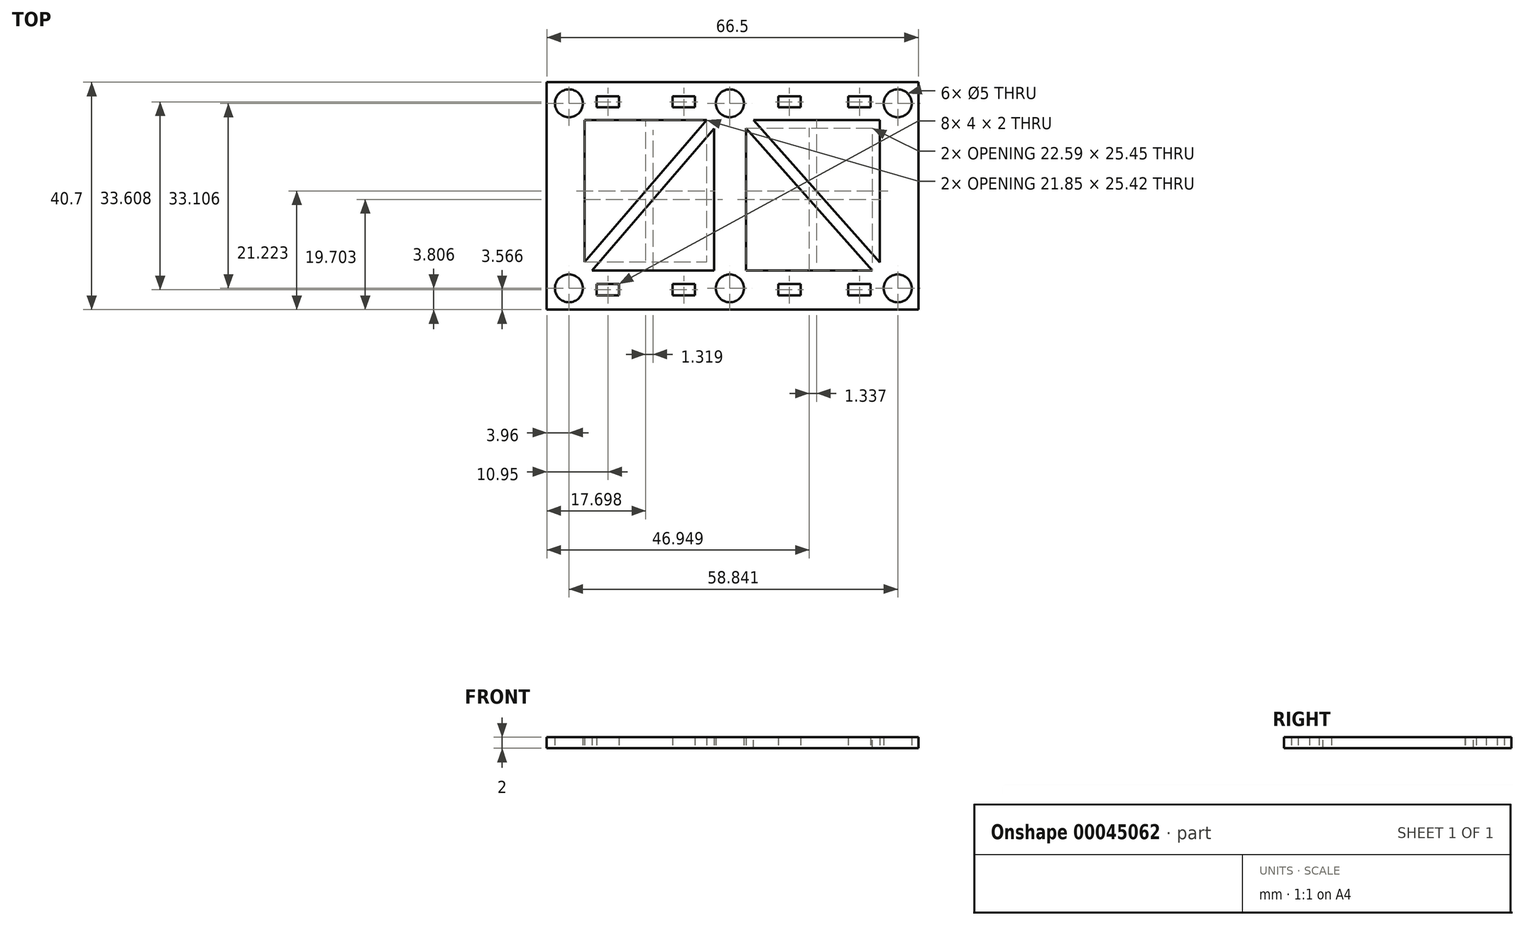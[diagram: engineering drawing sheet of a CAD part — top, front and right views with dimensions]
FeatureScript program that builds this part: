
annotation { "Feature Type Name" : "Feature", "Feature Type Description" : "" }
export const myFeature = defineFeature(function(context is Context, id is Id, definition is map)
    precondition{}
    {
        {
            var Q0;
            Q0=qCreatedBy(makeId("Top.planeOp"),FACE);
            var sketch = newSketch(context, id + "F0", { "sketchPlane" : qUnion([Q0])});
            skLineSegment(sketch, "E0.bottom", {"start": v(-59.63, 9.38) * mm, "end": v(6.87, 9.38) * mm});
            skLineSegment(sketch, "E0.top", {"start": v(-59.63, -31.32) * mm, "end": v(6.87, -31.32) * mm});
            skLineSegment(sketch, "E0.left", {"start": v(-59.63, 9.38) * mm, "end": v(-59.63, -31.32) * mm});
            skLineSegment(sketch, "E0.right", {"start": v(6.87, 9.38) * mm, "end": v(6.87, -31.32) * mm});
            skLineSegment(sketch, "E1.bottom", {"start": v(-52.86, 2.61) * mm, "end": v(-29.69, 2.61) * mm});
            skLineSegment(sketch, "E1.top", {"start": v(-52.86, -24.34) * mm, "end": v(-29.69, -24.34) * mm});
            skLineSegment(sketch, "E1.left", {"start": v(-52.86, 2.61) * mm, "end": v(-52.86, -24.34) * mm});
            skLineSegment(sketch, "E1.right", {"start": v(-29.69, 2.61) * mm, "end": v(-29.69, -24.34) * mm});
            skLineSegment(sketch, "E2.bottom", {"start": v(-23.98, 2.61) * mm, "end": v(-0.05, 2.61) * mm});
            skLineSegment(sketch, "E2.left", {"start": v(-23.98, 2.61) * mm, "end": v(-23.98, -24.34) * mm});
            skLineSegment(sketch, "E2.right", {"start": v(-0.05, 2.61) * mm, "end": v(-0.05, -24.34) * mm});
            skLineSegment(sketch, "E2.top", {"start": v(-23.98, -24.34) * mm, "end": v(-0.05, -24.34) * mm});
            skCircle(sketch, "E3", {"center": v(-26.87, -27.51) * mm, "radius": 2.5 * mm});
            skLineSegment(sketch, "E4", {"start": v(-52.86, -24.34) * mm, "end": v(-29.69, 2.61) * mm});
            skLineSegment(sketch, "E5", {"start": v(-23.98, 2.61) * mm, "end": v(-0.05, -24.34) * mm});
            skCircle(sketch, "E6", {"center": v(-55.67, -27.51) * mm, "radius": 2.5 * mm});
            skCircle(sketch, "E7", {"center": v(-55.67, 5.6) * mm, "radius": 2.5 * mm});
            skCircle(sketch, "E8", {"center": v(-26.87, 5.6) * mm, "radius": 2.5 * mm});
            skCircle(sketch, "E9", {"center": v(3.17, 5.6) * mm, "radius": 2.5 * mm});
            skCircle(sketch, "E10", {"center": v(3.17, -27.51) * mm, "radius": 2.5 * mm});
            skLineSegment(sketch, "E11.bottom", {"start": v(-50.68, 4.85) * mm, "end": v(-46.68, 4.85) * mm});
            skLineSegment(sketch, "E11.top", {"start": v(-50.68, 6.85) * mm, "end": v(-46.68, 6.85) * mm});
            skLineSegment(sketch, "E11.left", {"start": v(-50.68, 4.85) * mm, "end": v(-50.68, 6.85) * mm});
            skLineSegment(sketch, "E11.right", {"start": v(-46.68, 4.85) * mm, "end": v(-46.68, 6.85) * mm});
            skLineSegment(sketch, "E12.bottom", {"start": v(-50.68, -28.75) * mm, "end": v(-46.68, -28.75) * mm});
            skLineSegment(sketch, "E12.top", {"start": v(-50.68, -26.75) * mm, "end": v(-46.68, -26.75) * mm});
            skLineSegment(sketch, "E12.left", {"start": v(-50.68, -28.75) * mm, "end": v(-50.68, -26.75) * mm});
            skLineSegment(sketch, "E12.right", {"start": v(-46.68, -28.75) * mm, "end": v(-46.68, -26.75) * mm});
            skLineSegment(sketch, "E13.left", {"start": v(-5.66, 39.04) * mm, "end": v(-5.66, 40.7) * mm});
            skLineSegment(sketch, "E13.right", {"start": v(-1.66, 39.04) * mm, "end": v(-1.66, 40.7) * mm});
            skLineSegment(sketch, "E13.bottom", {"start": v(-5.66, 39.04) * mm, "end": v(-1.66, 39.04) * mm});
            skLineSegment(sketch, "E13.top", {"start": v(-5.66, 40.7) * mm, "end": v(-1.66, 40.7) * mm});
            skLineSegment(sketch, "E14.left", {"start": v(-5.66, 4.85) * mm, "end": v(-5.66, 6.85) * mm});
            skLineSegment(sketch, "E14.right", {"start": v(-1.66, 4.85) * mm, "end": v(-1.66, 6.85) * mm});
            skLineSegment(sketch, "E14.top", {"start": v(-5.66, 6.85) * mm, "end": v(-1.66, 6.85) * mm});
            skLineSegment(sketch, "E14.bottom", {"start": v(-5.66, 4.85) * mm, "end": v(-1.66, 4.85) * mm});
            skLineSegment(sketch, "E15.left", {"start": v(-5.66, -28.75) * mm, "end": v(-5.66, -26.75) * mm});
            skLineSegment(sketch, "E15.right", {"start": v(-1.66, -28.75) * mm, "end": v(-1.66, -26.75) * mm});
            skLineSegment(sketch, "E15.bottom", {"start": v(-5.66, -28.75) * mm, "end": v(-1.66, -28.75) * mm});
            skLineSegment(sketch, "E15.top", {"start": v(-5.66, -26.75) * mm, "end": v(-1.66, -26.75) * mm});
            skLineSegment(sketch, "E16.left", {"start": v(-5.66, -62.62) * mm, "end": v(-5.66, -60.97) * mm});
            skLineSegment(sketch, "E16.right", {"start": v(-1.66, -62.62) * mm, "end": v(-1.66, -60.97) * mm});
            skLineSegment(sketch, "E16.top", {"start": v(-5.66, -60.97) * mm, "end": v(-1.66, -60.97) * mm});
            skLineSegment(sketch, "E16.bottom", {"start": v(-5.66, -62.62) * mm, "end": v(-1.66, -62.62) * mm});
            skLineSegment(sketch, "E17.top", {"start": v(-37.1, 6.85) * mm, "end": v(-33.1, 6.85) * mm});
            skLineSegment(sketch, "E17.right", {"start": v(-33.1, 4.85) * mm, "end": v(-33.1, 6.85) * mm});
            skLineSegment(sketch, "E17.bottom", {"start": v(-37.1, 4.85) * mm, "end": v(-33.1, 4.85) * mm});
            skLineSegment(sketch, "E17.left", {"start": v(-37.1, 4.85) * mm, "end": v(-37.1, 6.85) * mm});
            skLineSegment(sketch, "E18.top", {"start": v(-37.1, -26.75) * mm, "end": v(-33.1, -26.75) * mm});
            skLineSegment(sketch, "E18.right", {"start": v(-33.1, -28.75) * mm, "end": v(-33.1, -26.75) * mm});
            skLineSegment(sketch, "E18.bottom", {"start": v(-37.1, -28.75) * mm, "end": v(-33.1, -28.75) * mm});
            skLineSegment(sketch, "E18.left", {"start": v(-37.1, -28.75) * mm, "end": v(-37.1, -26.75) * mm});
            skLineSegment(sketch, "E19.top", {"start": v(-18.21, 6.85) * mm, "end": v(-14.21, 6.85) * mm});
            skLineSegment(sketch, "E19.right", {"start": v(-14.21, 4.85) * mm, "end": v(-14.21, 6.85) * mm});
            skLineSegment(sketch, "E19.bottom", {"start": v(-18.21, 4.85) * mm, "end": v(-14.21, 4.85) * mm});
            skLineSegment(sketch, "E19.left", {"start": v(-18.21, 4.85) * mm, "end": v(-18.21, 6.85) * mm});
            skLineSegment(sketch, "E20.top", {"start": v(-18.21, -26.75) * mm, "end": v(-14.21, -26.75) * mm});
            skLineSegment(sketch, "E20.right", {"start": v(-14.21, -28.75) * mm, "end": v(-14.21, -26.75) * mm});
            skLineSegment(sketch, "E20.bottom", {"start": v(-18.21, -28.75) * mm, "end": v(-14.21, -28.75) * mm});
            skLineSegment(sketch, "E20.left", {"start": v(-18.21, -28.75) * mm, "end": v(-18.21, -26.75) * mm});
            skSolve(sketch);
        }
        {
            var Q0;
            Q0 = qSketchRegion(id + "F0", true);
            var Q1;
            Q1=makeQuery(id+"F0.imprint","IMPRINT",FACE,{"disambiguationData":[TD([[makeQuery(id+"F0.imprint","IMPRINT",EDGE,{"derivedFrom":sQuery(id+"F0.wireOp",EDGE,"E0.bottom")}),-1.0]])]});
            extrude(context, id + "F1", {"entities" : qUnion([Q0, Q1]), "depth" : 2 * mm});
        }
        {
            var Q0;
            Q0=sQuery(id+"F0.wireOp",EDGE,"E4");
            extrude(context, id + "F2", {"bodyType" : ToolBodyType.SURFACE, "surfaceEntities" : qUnion([Q0]), "depth" : 2 * mm});
        }
        {
            var Q0;
            Q0=makeQuery(id+"F2.opExtrude","SWEPT_FACE",FACE,{"disambiguationData":[OSD([sQuery(id+"F0.wireOp",EDGE,"E4")])]});
            extrude(context, id + "F3", {"entities" : qUnion([Q0]), "operationType" : NewBodyOperationType.ADD, "endBound" : BoundingType.SYMMETRIC, "depth" : 2 * mm});
        }
        {
            var Q0;
            Q0=sQuery(id+"F0.wireOp",EDGE,"E5");
            extrude(context, id + "F4", {"bodyType" : ToolBodyType.SURFACE, "surfaceEntities" : qUnion([Q0]), "depth" : 2 * mm});
        }
        {
            var Q0;
            Q0=makeQuery(id+"F4.opExtrude","SWEPT_FACE",FACE,{"disambiguationData":[OSD([sQuery(id+"F0.wireOp",EDGE,"E5")])]});
            extrude(context, id + "F5", {"entities" : qUnion([Q0]), "operationType" : NewBodyOperationType.ADD, "endBound" : BoundingType.SYMMETRIC, "depth" : 2 * mm});
        }
        {
            var Q0;
            Q0=makeQuery(id+"F1.opExtrude","SWEPT_BODY",BODY,{"disambiguationData":[OSD([sQuery(id+"F0.wireOp",EDGE,"E16.left"),sQuery(id+"F0.wireOp",EDGE,"E16.right"),sQuery(id+"F0.wireOp",EDGE,"E16.top"),sQuery(id+"F0.wireOp",EDGE,"E16.bottom")])]});
            deleteBodies(context, id + "F6", {"entities" : qUnion([Q0])});
        }
        {
            var Q0;
            Q0=makeQuery(id+"F1.opExtrude","SWEPT_BODY",BODY,{"disambiguationData":[OSD([sQuery(id+"F0.wireOp",EDGE,"E13.left"),sQuery(id+"F0.wireOp",EDGE,"E13.right"),sQuery(id+"F0.wireOp",EDGE,"E13.bottom"),sQuery(id+"F0.wireOp",EDGE,"E13.top")])]});
            deleteBodies(context, id + "F7", {"entities" : qUnion([Q0])});
        }
    });
